# Revit family: Drain_Receptor_Deck_15-Inch_Round_Zurn-Z108
name_source: partatom
category: Plumbing Fixtures
units: mm (PartAtom-declared; Revit-internal decimal feet)

## family parameters
Always vertical = Yes
Cut with Voids When Loaded = No
Maintain Annotation Orientation = No
OmniClass Number = 23.70.50.21.24.11
OmniClass Title = Roof Waste Water Drains
Part Type = Normal
Room Calculation Point = No
Round Connector Dimension = Use Radius
Shared = No
Work Plane-Based = No

## types (16) — shared parameters
Assembly Code = D2040200
CW Connection = No
Default Elevation = 20 "
Description = 15 INCH DIAMETER DECK RECEPTOR
Dome Open Area (Sq. In.) = 53 SF
HW Connection = No
Main Material = Iron - Zurn - Cast - Painted - Blue
Manufacturer = Zurn Water, LLC
Manufacurer Brand = Zurn
Model = Z108
Modified Date = 12/30/25
Product Documentation Link = https://files.zurn.com
Product Installation Sheet URL = https://files.zurn.com
Product Page URL = https://www.zurn.com
Product data url = https://www.bimobject.com
URL = www.zurn.com
Vent Connection = No
WFU = 1
Waste Connection = Yes
zero-valued in all types: CWFU, HWFU

## per-type parameters (varying)
| type | Approx. Weight (Lbs) | Body HT Dim 'E' | Pipe Size 'A' (Inner Diameter) | Pipe Size 'A' (Inner Radius) | Pipe Size 'A' (Nominal Diameter) | Pipe Size 'A' (Nominal Radius) | Pipe Size 'A' (Outer Diameter) | Pipe Size 'A' (Outer Radius) | Type Comments |
| Z108-3IC | 41 " | 5.25 " | 3.068 " | 1.534 " | 3 " | 1.5 " | 3.5 " | 1.75 " | Z108 - 2 Inch Inside Caulk Outlet |
| Z108-4IC | 41 " | 5.25 " | 4.028 " | 2.014 " | 4 " | 2 " | 4.5 " | 2.25 " | Z108 - 4 Inch Inside Caulk Outlet |
| Z108-6IC | 39 " | 5.25 " | 6.065 " | 3.033 " | 6 " | 3 " | 6.625 " | 3.313 " | Z108 - 6 Inch Inside Caulk Outlet |
| Z108-2IP | 41 " | 3.75 " | 2.067 " | 1.034 " | 2 " | 1 " | 2.375 " | 1.188 " | Z108 - 2 Inch Threaded Outlet |
| Z108-3IP | 41 " | 3.75 " | 3.068 " | 1.534 " | 3 " | 1.5 " | 3.5 " | 1.75 " | Z108 - 2 Inch Threaded Outlet |
| Z108-4IP | 41 " | 3.75 " | 4.028 " | 2.014 " | 4 " | 2 " | 4.5 " | 2.25 " | Z108 - 4 Inch Threaded Outlet |
| Z108-6IP | 39 " | 3.75 " | 6.065 " | 3.033 " | 6 " | 3 " | 6.625 " | 3.313 " | Z108 - 6 Inch Threaded Outlet |
| Z108-8IP | 42 " | 3.75 " | 7.98 " | 3.99 " | 8 " | 4 " | 8.625 " | 4.313 " | Z108 - 8 Inch Threaded Outlet |
| Z108-2NH | 41 " | 5.25 " | 2.067 " | 1.034 " | 2 " | 1 " | 2.375 " | 1.188 " | Z108 - 2 Inch No-Hub outlet |
| Z108-3NH | 41 " | 5.25 " | 3.068 " | 1.534 " | 3 " | 1.5 " | 3.5 " | 1.75 " | Z108 - 2 Inch No-Hub outlet |
| Z108-4NH | 41 " | 5.25 " | 4.028 " | 2.014 " | 4 " | 2 " | 4.5 " | 2.25 " | Z108 - 4 Inch No-Hub outlet |
| Z108-6NH | 39 " | 5.25 " | 6.065 " | 3.033 " | 6 " | 3 " | 6.625 " | 3.313 " | Z108 - 6 Inch No-Hub outlet |
| Z108-8NH | 42 " | 5.25 " | 7.98 " | 3.99 " | 8 " | 4 " | 8.625 " | 4.313 " | Z108 - 8 Inch No-Hub outlet |
| Z108-2NL | 41 " | 4.563 " | 2.067 " | 1.034 " | 2 " | 1 " | 2.375 " | 1.188 " | Z108 - 2 Inch Neo-Loc Outlet |
| Z108-3NL | 41 " | 4.563 " | 3.068 " | 1.534 " | 3 " | 1.5 " | 3.5 " | 1.75 " | Z108 - 2 Inch Neo-Loc Outlet |
| Z108-4NL | 41 " | 4.563 " | 4.028 " | 2.014 " | 4 " | 2 " | 4.5 " | 2.25 " | Z108 - 4 Inch Neo-Loc Outlet |

## geometry (parser evidence)
native form markers: Blend x6, Sweep x5
no freeform markers — native parametric forms only
